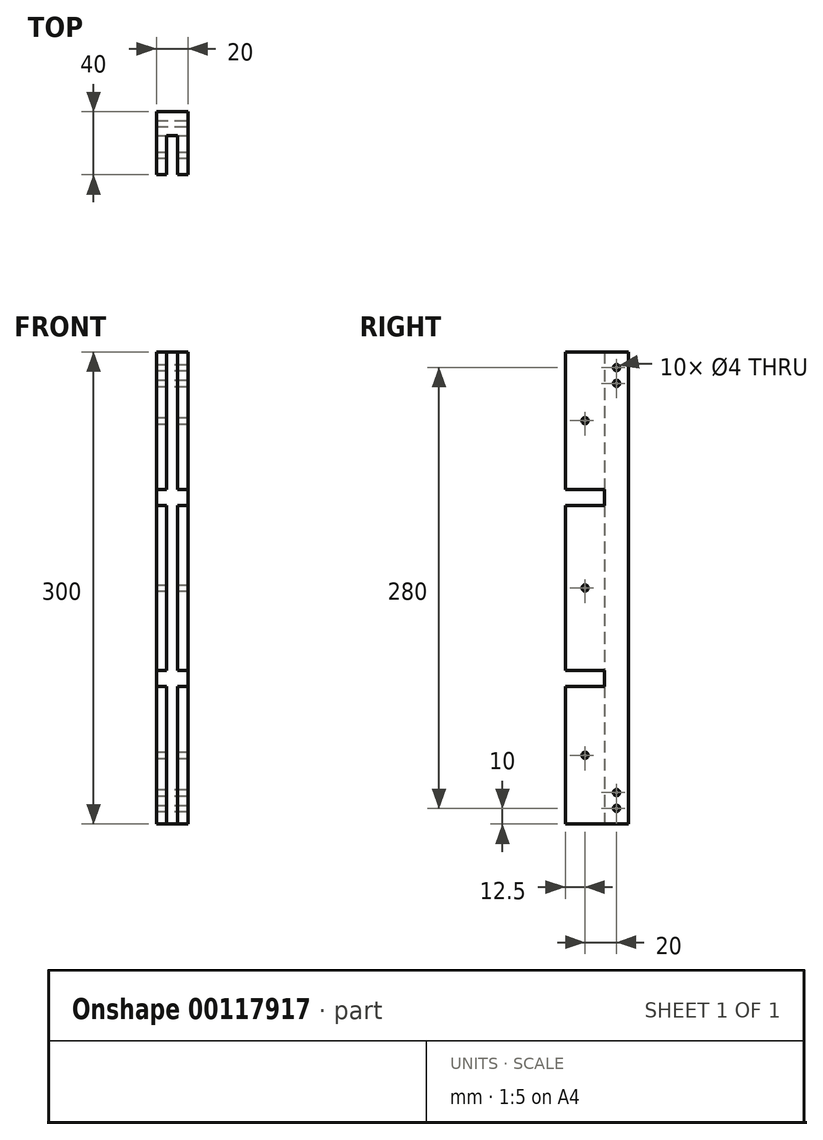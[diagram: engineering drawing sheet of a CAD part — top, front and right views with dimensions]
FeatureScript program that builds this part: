
annotation { "Feature Type Name" : "Feature", "Feature Type Description" : "" }
export const myFeature = defineFeature(function(context is Context, id is Id, definition is map)
    precondition{}
    {
        {
            var Q0;
            Q0=qCreatedBy(makeId("Top.planeOp"),FACE);
            var sketch = newSketch(context, id + "F0", { "sketchPlane" : qUnion([Q0])});
            skLineSegment(sketch, "E0.top", {"start": v(0, 40) * mm, "end": v(20, 40) * mm});
            skLineSegment(sketch, "E0.left", {"start": v(0, 0) * mm, "end": v(0, 40) * mm});
            skLineSegment(sketch, "E0.right", {"start": v(20, 0) * mm, "end": v(20, 40) * mm});
            skLineSegment(sketch, "E1", {"start": v(0, 0) * mm, "end": v(6.5, 0) * mm});
            skLineSegment(sketch, "E2", {"start": v(6.5, 0) * mm, "end": v(6.5, 25) * mm});
            skLineSegment(sketch, "E3", {"start": v(6.5, 25) * mm, "end": v(13.5, 25) * mm});
            skLineSegment(sketch, "E4", {"start": v(13.5, 25) * mm, "end": v(13.5, 0) * mm});
            skLineSegment(sketch, "E5", {"start": v(13.5, 0) * mm, "end": v(20, 0) * mm});
            skSolve(sketch);
        }
        {
            var Q0;
            Q0 = qSketchRegion(id + "F0", true);
            extrude(context, id + "F1", {"entities" : qUnion([Q0]), "depth" : 300 * mm});
        }
        {
            var Q0;
            Q0=makeQuery(id+"F1.opExtrude","SWEPT_FACE",FACE,{"disambiguationData":[OSD([sQuery(id+"F0.wireOp",EDGE,"E0.right")])]});
            var sketch = newSketch(context, id + "F2", { "sketchPlane" : qUnion([Q0])});
            skLineSegment(sketch, "E6", {"start": v(0, 212.5) * mm, "end": v(25, 212.5) * mm});
            skLineSegment(sketch, "E7", {"start": v(25, 212.5) * mm, "end": v(25, 202.5) * mm});
            skLineSegment(sketch, "E8", {"start": v(25, 202.5) * mm, "end": v(0, 202.5) * mm});
            skLineSegment(sketch, "E9", {"start": v(0, 97.5) * mm, "end": v(25, 97.5) * mm});
            skLineSegment(sketch, "E10", {"start": v(25, 97.5) * mm, "end": v(25, 87.5) * mm});
            skLineSegment(sketch, "E11", {"start": v(25, 87.5) * mm, "end": v(0, 87.5) * mm});
            skLineSegment(sketch, "E12", {"start": v(25, 212.5) * mm, "end": v(25, 300) * mm, "construction": true});
            skLineSegment(sketch, "E13", {"start": v(25, 87.5) * mm, "end": v(25, 0) * mm, "construction": true});
            skCircle(sketch, "E14", {"center": v(12.5, 256.25) * mm, "radius": 2 * mm});
            skCircle(sketch, "E15", {"center": v(12.5, 150) * mm, "radius": 2 * mm});
            skCircle(sketch, "E16", {"center": v(12.5, 43.75) * mm, "radius": 2 * mm});
            skCircle(sketch, "E17", {"center": v(32.5, 290) * mm, "radius": 2 * mm});
            skCircle(sketch, "E18", {"center": v(32.5, 10) * mm, "radius": 2 * mm});
            skLineSegment(sketch, "E19", {"start": v(25, 202.5) * mm, "end": v(25, 97.5) * mm, "construction": true});
            skLineSegment(sketch, "E20", {"start": v(25, 256.25) * mm, "end": v(0, 256.25) * mm, "construction": true});
            skLineSegment(sketch, "E21", {"start": v(25, 150) * mm, "end": v(0, 150) * mm, "construction": true});
            skLineSegment(sketch, "E22", {"start": v(25, 43.75) * mm, "end": v(0, 43.75) * mm, "construction": true});
            skCircle(sketch, "E23", {"center": v(32.5, 280) * mm, "radius": 2 * mm});
            skCircle(sketch, "E24", {"center": v(32.5, 20) * mm, "radius": 2 * mm});
            skSolve(sketch);
        }
        {
            var Q0;
            {var subQ0=sQuery(id+"F2.wireOp",EDGE,"E6");Q0=makeQuery(id+"F2.imprint","IMPRINT",FACE,{"disambiguationData":[TD([[makeQuery(id+"F2.imprint","IMPRINT",EDGE,{"derivedFrom":subQ0}),-1.0]])]});}
            var Q1;
            {var subQ0=sQuery(id+"F2.wireOp",EDGE,"E9");Q1=makeQuery(id+"F2.imprint","IMPRINT",FACE,{"disambiguationData":[TD([[makeQuery(id+"F2.imprint","IMPRINT",EDGE,{"derivedFrom":subQ0}),-1.0]])]});}
            var Q2;
            Q2=makeQuery(id+"F2.imprint","IMPRINT",FACE,{"disambiguationData":[TD([[makeQuery(id+"F2.imprint","IMPRINT",EDGE,{"derivedFrom":sQuery(id+"F2.wireOp",EDGE,"E14")}),1.0]])]});
            var Q3;
            Q3=makeQuery(id+"F2.imprint","IMPRINT",FACE,{"disambiguationData":[TD([[makeQuery(id+"F2.imprint","IMPRINT",EDGE,{"derivedFrom":sQuery(id+"F2.wireOp",EDGE,"E23")}),1.0]])]});
            var Q4;
            Q4=makeQuery(id+"F2.imprint","IMPRINT",FACE,{"disambiguationData":[TD([[makeQuery(id+"F2.imprint","IMPRINT",EDGE,{"derivedFrom":sQuery(id+"F2.wireOp",EDGE,"E17")}),1.0]])]});
            var Q5;
            Q5=makeQuery(id+"F2.imprint","IMPRINT",FACE,{"disambiguationData":[TD([[makeQuery(id+"F2.imprint","IMPRINT",EDGE,{"derivedFrom":sQuery(id+"F2.wireOp",EDGE,"E15")}),1.0]])]});
            var Q6;
            Q6=makeQuery(id+"F2.imprint","IMPRINT",FACE,{"disambiguationData":[TD([[makeQuery(id+"F2.imprint","IMPRINT",EDGE,{"derivedFrom":sQuery(id+"F2.wireOp",EDGE,"E16")}),1.0]])]});
            var Q7;
            Q7=makeQuery(id+"F2.imprint","IMPRINT",FACE,{"disambiguationData":[TD([[makeQuery(id+"F2.imprint","IMPRINT",EDGE,{"derivedFrom":sQuery(id+"F2.wireOp",EDGE,"E24")}),1.0]])]});
            var Q8;
            Q8=makeQuery(id+"F2.imprint","IMPRINT",FACE,{"disambiguationData":[TD([[makeQuery(id+"F2.imprint","IMPRINT",EDGE,{"derivedFrom":sQuery(id+"F2.wireOp",EDGE,"E18")}),1.0]])]});
            extrude(context, id + "F3", {"entities" : qUnion([Q0, Q1, Q2, Q3, Q4, Q5, Q6, Q7, Q8]), "operationType" : NewBodyOperationType.REMOVE, "endBound" : BoundingType.THROUGH_ALL, "oppositeDirection" : true, "depth" : 25 * mm});
        }
    });
